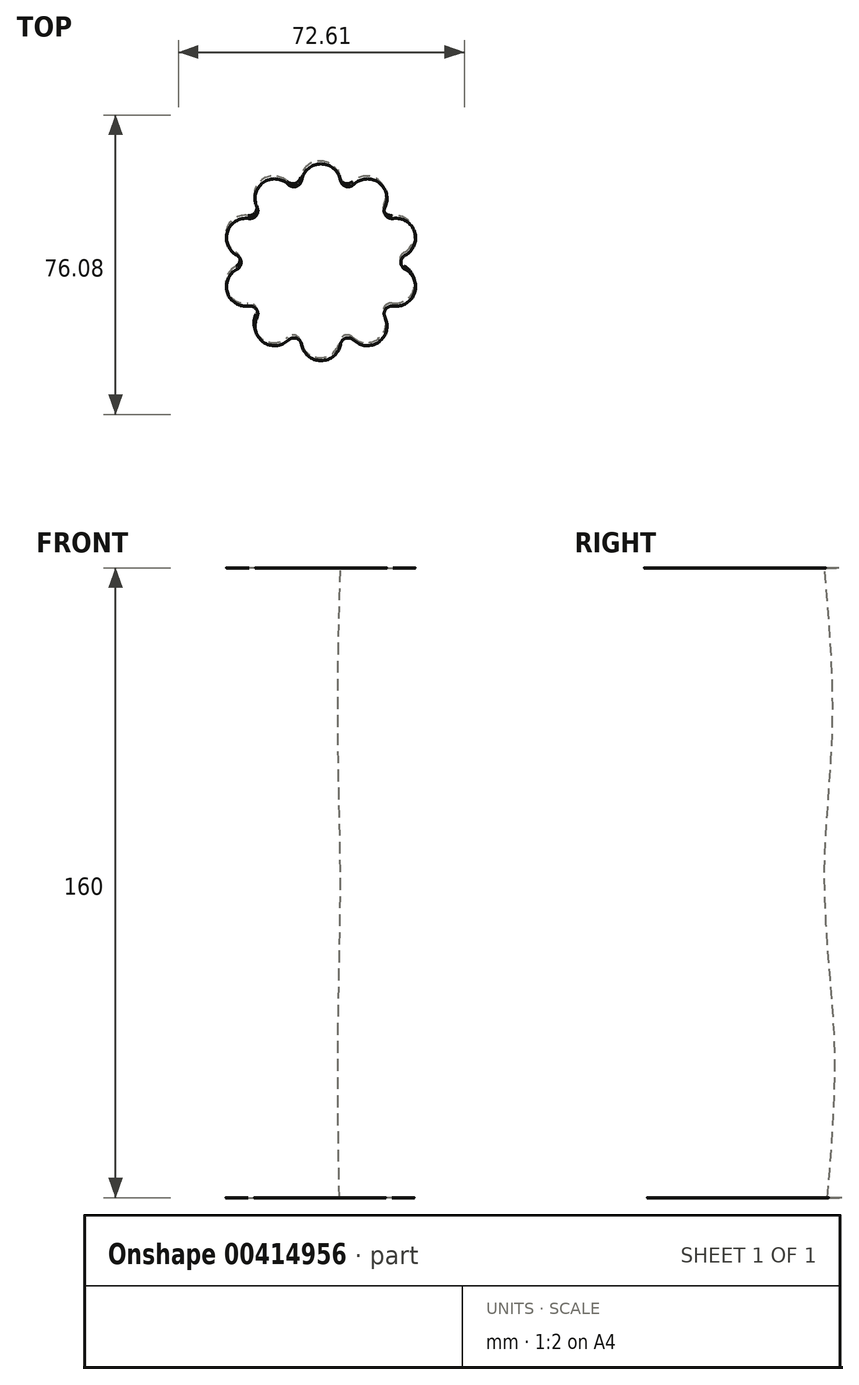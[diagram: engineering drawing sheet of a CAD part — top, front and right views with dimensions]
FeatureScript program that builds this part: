
annotation { "Feature Type Name" : "Feature", "Feature Type Description" : "" }
export const myFeature = defineFeature(function(context is Context, id is Id, definition is map)
    precondition{}
    {
        {
            var Q0;
            Q0=qCreatedBy(makeId("Top.planeOp"),FACE);
            var sketch = newSketch(context, id + "F0", { "sketchPlane" : qUnion([Q0])});
            skCircle(sketch, "E0", {"center": v(0, 20) * mm, "radius": 5 * mm});
            skCircle(sketch, "E1.1.0", {"center": v(11.76, 16.18) * mm, "radius": 5 * mm});
            skCircle(sketch, "E1.2.0", {"center": v(19.02, 6.18) * mm, "radius": 5 * mm});
            skCircle(sketch, "E1.3.0", {"center": v(19.02, -6.18) * mm, "radius": 5 * mm});
            skCircle(sketch, "E1.4.0", {"center": v(11.76, -16.18) * mm, "radius": 5 * mm});
            skCircle(sketch, "E1.5.0", {"center": v(0, -20) * mm, "radius": 5 * mm});
            skCircle(sketch, "E1.6.0", {"center": v(-11.76, -16.18) * mm, "radius": 5 * mm});
            skCircle(sketch, "E1.7.0", {"center": v(-19.02, -6.18) * mm, "radius": 5 * mm});
            skPoint(sketch, "E1.center", {"position": v(0, 0) * mm});
            skLineSegment(sketch, "E1.anchor1", {"start": v(0, 0) * mm, "end": v(0, 20) * mm, "construction": true});
            skLineSegment(sketch, "E1.anchor2", {"start": v(0, 0) * mm, "end": v(-11.76, 16.18) * mm, "construction": true});
            skCircle(sketch, "E2.1.8.0", {"center": v(-19.02, 6.18) * mm, "radius": 5 * mm});
            skCircle(sketch, "E2.1.9.0", {"center": v(-11.76, 16.18) * mm, "radius": 5 * mm});
            skArc(sketch, "E3", {"start": v(4.92, 20.86) * mm, "mid": v(6.27, 19.31) * mm, "end": v(8.28, 19.77) * mm});
            skArc(sketch, "E4.1.0", {"start": v(-8.28, 19.77) * mm, "mid": v(-6.27, 19.31) * mm, "end": v(-4.92, 20.86) * mm});
            skArc(sketch, "E4.2.0", {"start": v(-18.32, 11.13) * mm, "mid": v(-16.43, 11.93) * mm, "end": v(-16.25, 13.98) * mm});
            skArc(sketch, "E4.3.0", {"start": v(-21.36, -1.76) * mm, "mid": v(-20.3, 0) * mm, "end": v(-21.36, 1.76) * mm});
            skArc(sketch, "E4.4.0", {"start": v(-16.25, -13.98) * mm, "mid": v(-16.43, -11.93) * mm, "end": v(-18.32, -11.13) * mm});
            skArc(sketch, "E4.5.0", {"start": v(-4.92, -20.86) * mm, "mid": v(-6.27, -19.31) * mm, "end": v(-8.28, -19.77) * mm});
            skArc(sketch, "E4.6.0", {"start": v(8.28, -19.77) * mm, "mid": v(6.27, -19.31) * mm, "end": v(4.92, -20.86) * mm});
            skArc(sketch, "E4.7.0", {"start": v(18.32, -11.13) * mm, "mid": v(16.43, -11.93) * mm, "end": v(16.25, -13.98) * mm});
            skArc(sketch, "E4.8.0", {"start": v(21.36, 1.76) * mm, "mid": v(20.3, 0) * mm, "end": v(21.36, -1.76) * mm});
            skArc(sketch, "E4.9.0", {"start": v(16.25, 13.98) * mm, "mid": v(16.43, 11.93) * mm, "end": v(18.32, 11.13) * mm});
            skSolve(sketch);
        }
        {
            var Q0;
            Q0=qCreatedBy(makeId("Top.planeOp"),FACE);
            cPlane(context, id + "F1", {"entities" : qUnion([Q0]), "cplaneType" : CPlaneType.OFFSET, "offset" : 40 * mm, "width" : 150 * mm, "height" : 150 * mm});
        }
        {
            var Q0;
            Q0=qCreatedBy(id+"F1.planeOp",FACE);
            cPlane(context, id + "F2", {"entities" : qUnion([Q0]), "cplaneType" : CPlaneType.OFFSET, "offset" : 40 * mm, "width" : 150 * mm, "height" : 150 * mm});
        }
        {
            var Q0;
            Q0=qCreatedBy(id+"F2.planeOp",FACE);
            cPlane(context, id + "F3", {"entities" : qUnion([Q0]), "cplaneType" : CPlaneType.OFFSET, "offset" : 40 * mm, "width" : 150 * mm, "height" : 150 * mm});
        }
        {
            var Q0;
            Q0=qCreatedBy(id+"F3.planeOp",FACE);
            cPlane(context, id + "F4", {"entities" : qUnion([Q0]), "cplaneType" : CPlaneType.OFFSET, "offset" : 40 * mm, "width" : 150 * mm, "height" : 150 * mm});
        }
        {
            var Q0;
            Q0=qCreatedBy(id+"F1.planeOp",FACE);
            var sketch = newSketch(context, id + "F5", { "sketchPlane" : qUnion([Q0])});
            skCircle(sketch, "E5", {"center": v(0.37, 28.87) * mm, "radius": 7.5 * mm});
            skCircle(sketch, "E6.1.0", {"center": v(18, 23.14) * mm, "radius": 7.5 * mm});
            skCircle(sketch, "E6.2.0", {"center": v(28.9, 8.14) * mm, "radius": 7.5 * mm});
            skCircle(sketch, "E6.3.0", {"center": v(28.9, -10.4) * mm, "radius": 7.5 * mm});
            skCircle(sketch, "E6.4.0", {"center": v(18, -25.4) * mm, "radius": 7.5 * mm});
            skCircle(sketch, "E6.5.0", {"center": v(0.37, -31.13) * mm, "radius": 7.5 * mm});
            skCircle(sketch, "E6.6.0", {"center": v(-17.27, -25.4) * mm, "radius": 7.5 * mm});
            skCircle(sketch, "E6.7.0", {"center": v(-28.16, -10.4) * mm, "radius": 7.5 * mm});
            skPoint(sketch, "E6.center", {"position": v(0.37, -1.13) * mm});
            skLineSegment(sketch, "E6.anchor1", {"start": v(0.37, -1.13) * mm, "end": v(0.37, 28.87) * mm, "construction": true});
            skLineSegment(sketch, "E6.anchor2", {"start": v(0.37, -1.13) * mm, "end": v(-17.27, 23.14) * mm, "construction": true});
            skCircle(sketch, "E7.1.8.0", {"center": v(-28.16, 8.14) * mm, "radius": 7.5 * mm});
            skCircle(sketch, "E7.1.9.0", {"center": v(-17.27, 23.14) * mm, "radius": 7.5 * mm});
            skArc(sketch, "E8", {"start": v(4.56, 22.65) * mm, "mid": v(5.62, 15.05) * mm, "end": v(10.95, 20.57) * mm});
            skArc(sketch, "E9.1.0", {"start": v(-10.22, 20.57) * mm, "mid": v(-4.89, 15.05) * mm, "end": v(-3.82, 22.65) * mm});
            skArc(sketch, "E9.2.0", {"start": v(-20.95, 10.2) * mm, "mid": v(-13.4, 8.87) * mm, "end": v(-17, 15.64) * mm});
            skArc(sketch, "E9.3.0", {"start": v(-23.54, -4.5) * mm, "mid": v(-16.64, -1.13) * mm, "end": v(-23.54, 2.23) * mm});
            skArc(sketch, "E9.4.0", {"start": v(-17, -17.9) * mm, "mid": v(-13.4, -11.13) * mm, "end": v(-20.95, -12.46) * mm});
            skArc(sketch, "E9.5.0", {"start": v(-3.82, -24.91) * mm, "mid": v(-4.89, -17.3) * mm, "end": v(-10.22, -22.83) * mm});
            skArc(sketch, "E9.6.0", {"start": v(10.95, -22.83) * mm, "mid": v(5.62, -17.3) * mm, "end": v(4.56, -24.91) * mm});
            skArc(sketch, "E9.7.0", {"start": v(21.69, -12.46) * mm, "mid": v(14.13, -11.13) * mm, "end": v(17.73, -17.9) * mm});
            skArc(sketch, "E9.8.0", {"start": v(24.28, 2.23) * mm, "mid": v(17.38, -1.13) * mm, "end": v(24.28, -4.5) * mm});
            skArc(sketch, "E9.9.0", {"start": v(17.73, 15.64) * mm, "mid": v(14.13, 8.87) * mm, "end": v(21.69, 10.2) * mm});
            skLineSegment(sketch, "E10.0", {"start": v(0.37, -1.13) * mm, "end": v(0.37, -1.13) * mm});
            skSolve(sketch);
        }
        {
            var Q0;
            Q0=qCreatedBy(id+"F2.planeOp",FACE);
            var sketch = newSketch(context, id + "F6", { "sketchPlane" : qUnion([Q0])});
            skCircle(sketch, "E11", {"center": v(0.24, 19.25) * mm, "radius": 5 * mm});
            skCircle(sketch, "E12.1.0", {"center": v(12, 15.43) * mm, "radius": 5 * mm});
            skCircle(sketch, "E12.2.0", {"center": v(19.27, 5.43) * mm, "radius": 5 * mm});
            skCircle(sketch, "E12.3.0", {"center": v(19.27, -6.93) * mm, "radius": 5 * mm});
            skCircle(sketch, "E12.4.0", {"center": v(12, -16.93) * mm, "radius": 5 * mm});
            skCircle(sketch, "E12.5.0", {"center": v(0.24, -20.75) * mm, "radius": 5 * mm});
            skCircle(sketch, "E12.6.0", {"center": v(-11.51, -16.93) * mm, "radius": 5 * mm});
            skCircle(sketch, "E12.7.0", {"center": v(-18.78, -6.93) * mm, "radius": 5 * mm});
            skPoint(sketch, "E12.center", {"position": v(0.24, -0.75) * mm});
            skLineSegment(sketch, "E12.anchor1", {"start": v(0.24, -0.75) * mm, "end": v(0.24, 19.25) * mm, "construction": true});
            skLineSegment(sketch, "E12.anchor2", {"start": v(0.24, -0.75) * mm, "end": v(-11.51, 15.43) * mm, "construction": true});
            skCircle(sketch, "E13.1.8.0", {"center": v(-18.78, 5.43) * mm, "radius": 5 * mm});
            skCircle(sketch, "E13.1.9.0", {"center": v(-11.51, 15.43) * mm, "radius": 5 * mm});
            skArc(sketch, "E14", {"start": v(5.17, 20.1) * mm, "mid": v(6.52, 18.56) * mm, "end": v(8.52, 19.02) * mm});
            skArc(sketch, "E15.1.0", {"start": v(-8.03, 19.02) * mm, "mid": v(-6.03, 18.56) * mm, "end": v(-4.68, 20.1) * mm});
            skArc(sketch, "E15.2.0", {"start": v(-18.08, 10.38) * mm, "mid": v(-16.18, 11.18) * mm, "end": v(-16, 13.23) * mm});
            skArc(sketch, "E15.3.0", {"start": v(-21.12, -2.52) * mm, "mid": v(-20.06, -0.75) * mm, "end": v(-21.12, 1) * mm});
            skArc(sketch, "E15.4.0", {"start": v(-16, -14.74) * mm, "mid": v(-16.18, -12.69) * mm, "end": v(-18.08, -11.88) * mm});
            skArc(sketch, "E15.5.0", {"start": v(-4.68, -21.62) * mm, "mid": v(-6.03, -20.06) * mm, "end": v(-8.03, -20.53) * mm});
            skArc(sketch, "E15.6.0", {"start": v(8.52, -20.53) * mm, "mid": v(6.52, -20.06) * mm, "end": v(5.17, -21.62) * mm});
            skArc(sketch, "E15.7.0", {"start": v(18.57, -11.88) * mm, "mid": v(16.67, -12.69) * mm, "end": v(16.5, -14.74) * mm});
            skArc(sketch, "E15.8.0", {"start": v(21.6, 1) * mm, "mid": v(20.55, -0.75) * mm, "end": v(21.6, -2.52) * mm});
            skArc(sketch, "E15.9.0", {"start": v(16.5, 13.23) * mm, "mid": v(16.67, 11.18) * mm, "end": v(18.57, 10.38) * mm});
            skSolve(sketch);
        }
        {
            var Q0;
            Q0=qCreatedBy(id+"F3.planeOp",FACE);
            var sketch = newSketch(context, id + "F7", { "sketchPlane" : qUnion([Q0])});
            skCircle(sketch, "E16", {"center": v(0.34, 28.38) * mm, "radius": 7.5 * mm});
            skCircle(sketch, "E17.1.0", {"center": v(17.97, 22.65) * mm, "radius": 7.5 * mm});
            skCircle(sketch, "E17.2.0", {"center": v(28.87, 7.65) * mm, "radius": 7.5 * mm});
            skCircle(sketch, "E17.3.0", {"center": v(28.87, -10.9) * mm, "radius": 7.5 * mm});
            skCircle(sketch, "E17.4.0", {"center": v(17.97, -25.9) * mm, "radius": 7.5 * mm});
            skCircle(sketch, "E17.5.0", {"center": v(0.34, -31.62) * mm, "radius": 7.5 * mm});
            skCircle(sketch, "E17.6.0", {"center": v(-17.3, -25.9) * mm, "radius": 7.5 * mm});
            skCircle(sketch, "E17.7.0", {"center": v(-28.2, -10.9) * mm, "radius": 7.5 * mm});
            skPoint(sketch, "E17.center", {"position": v(0.34, -1.62) * mm});
            skLineSegment(sketch, "E17.anchor1", {"start": v(0.34, -1.62) * mm, "end": v(0.34, 28.38) * mm, "construction": true});
            skLineSegment(sketch, "E17.anchor2", {"start": v(0.34, -1.62) * mm, "end": v(-17.3, 22.65) * mm, "construction": true});
            skCircle(sketch, "E18.1.8.0", {"center": v(-28.2, 7.65) * mm, "radius": 7.5 * mm});
            skCircle(sketch, "E18.1.9.0", {"center": v(-17.3, 22.65) * mm, "radius": 7.5 * mm});
            skArc(sketch, "E19", {"start": v(4.53, 22.16) * mm, "mid": v(5.6, 14.56) * mm, "end": v(10.93, 20.08) * mm});
            skArc(sketch, "E20.1.0", {"start": v(-10.25, 20.08) * mm, "mid": v(-4.92, 14.56) * mm, "end": v(-3.85, 22.16) * mm});
            skArc(sketch, "E20.2.0", {"start": v(-20.98, 9.71) * mm, "mid": v(-13.42, 8.38) * mm, "end": v(-17.03, 15.15) * mm});
            skArc(sketch, "E20.3.0", {"start": v(-23.57, -4.98) * mm, "mid": v(-16.67, -1.62) * mm, "end": v(-23.57, 1.74) * mm});
            skArc(sketch, "E20.4.0", {"start": v(-17.03, -18.4) * mm, "mid": v(-13.42, -11.62) * mm, "end": v(-20.98, -12.95) * mm});
            skArc(sketch, "E20.5.0", {"start": v(-3.85, -25.4) * mm, "mid": v(-4.92, -17.8) * mm, "end": v(-10.25, -23.32) * mm});
            skArc(sketch, "E20.6.0", {"start": v(10.93, -23.32) * mm, "mid": v(5.6, -17.8) * mm, "end": v(4.53, -25.4) * mm});
            skArc(sketch, "E20.7.0", {"start": v(21.66, -12.95) * mm, "mid": v(14.1, -11.62) * mm, "end": v(17.7, -18.4) * mm});
            skArc(sketch, "E20.8.0", {"start": v(24.25, 1.74) * mm, "mid": v(17.35, -1.62) * mm, "end": v(24.25, -4.98) * mm});
            skArc(sketch, "E20.9.0", {"start": v(17.7, 15.15) * mm, "mid": v(14.1, 8.38) * mm, "end": v(21.66, 9.71) * mm});
            skLineSegment(sketch, "E21.0", {"start": v(0.34, -1.62) * mm, "end": v(0.34, -1.62) * mm});
            skSolve(sketch);
        }
        {
            var Q0;
            Q0=qCreatedBy(id+"F4.planeOp",FACE);
            var sketch = newSketch(context, id + "F8", { "sketchPlane" : qUnion([Q0])});
            skCircle(sketch, "E22", {"center": v(0.24, 19.25) * mm, "radius": 5 * mm});
            skCircle(sketch, "E23.1.0", {"center": v(12, 15.43) * mm, "radius": 5 * mm});
            skCircle(sketch, "E23.2.0", {"center": v(19.27, 5.43) * mm, "radius": 5 * mm});
            skCircle(sketch, "E23.3.0", {"center": v(19.27, -6.93) * mm, "radius": 5 * mm});
            skCircle(sketch, "E23.4.0", {"center": v(12, -16.93) * mm, "radius": 5 * mm});
            skCircle(sketch, "E23.5.0", {"center": v(0.24, -20.75) * mm, "radius": 5 * mm});
            skCircle(sketch, "E23.6.0", {"center": v(-11.51, -16.93) * mm, "radius": 5 * mm});
            skCircle(sketch, "E23.7.0", {"center": v(-18.78, -6.93) * mm, "radius": 5 * mm});
            skPoint(sketch, "E23.center", {"position": v(0.24, -0.75) * mm});
            skLineSegment(sketch, "E23.anchor1", {"start": v(0.24, -0.75) * mm, "end": v(0.24, 19.25) * mm, "construction": true});
            skLineSegment(sketch, "E23.anchor2", {"start": v(0.24, -0.75) * mm, "end": v(-11.51, 15.43) * mm, "construction": true});
            skCircle(sketch, "E24.1.8.0", {"center": v(-18.78, 5.43) * mm, "radius": 5 * mm});
            skCircle(sketch, "E24.1.9.0", {"center": v(-11.51, 15.43) * mm, "radius": 5 * mm});
            skArc(sketch, "E25", {"start": v(5.17, 20.1) * mm, "mid": v(6.52, 18.56) * mm, "end": v(8.52, 19.02) * mm});
            skArc(sketch, "E26.1.0", {"start": v(-8.03, 19.02) * mm, "mid": v(-6.03, 18.56) * mm, "end": v(-4.68, 20.1) * mm});
            skArc(sketch, "E26.2.0", {"start": v(-18.08, 10.38) * mm, "mid": v(-16.18, 11.18) * mm, "end": v(-16, 13.23) * mm});
            skArc(sketch, "E26.3.0", {"start": v(-21.12, -2.52) * mm, "mid": v(-20.06, -0.75) * mm, "end": v(-21.12, 1) * mm});
            skArc(sketch, "E26.4.0", {"start": v(-16, -14.74) * mm, "mid": v(-16.18, -12.69) * mm, "end": v(-18.08, -11.88) * mm});
            skArc(sketch, "E26.5.0", {"start": v(-4.68, -21.62) * mm, "mid": v(-6.03, -20.06) * mm, "end": v(-8.03, -20.53) * mm});
            skArc(sketch, "E26.6.0", {"start": v(8.52, -20.53) * mm, "mid": v(6.52, -20.06) * mm, "end": v(5.17, -21.62) * mm});
            skArc(sketch, "E26.7.0", {"start": v(18.57, -11.88) * mm, "mid": v(16.67, -12.69) * mm, "end": v(16.5, -14.74) * mm});
            skArc(sketch, "E26.8.0", {"start": v(21.6, 1) * mm, "mid": v(20.55, -0.75) * mm, "end": v(21.6, -2.52) * mm});
            skArc(sketch, "E26.9.0", {"start": v(16.5, 13.23) * mm, "mid": v(16.67, 11.18) * mm, "end": v(18.57, 10.38) * mm});
            skSolve(sketch);
        }
        {
            var Q0;
            Q0 = qSketchRegion(id + "F0", true);
            var Q1;
            Q1 = qSketchRegion(id + "F5", true);
            var Q2;
            Q2 = qSketchRegion(id + "F6", true);
            var Q3;
            Q3 = qSketchRegion(id + "F7", true);
            var Q4;
            Q4 = qSketchRegion(id + "F8", true);
            loft(context, id + "F9", {"sheetProfilesArray" : [{ "sheetProfileEntities" : qUnion([Q0]) }, { "sheetProfileEntities" : qUnion([Q1]) }, { "sheetProfileEntities" : qUnion([Q2]) }, { "sheetProfileEntities" : qUnion([Q3]) }, { "sheetProfileEntities" : qUnion([Q4]) }]});
        }
    });
